# Revit family: Window-NanaWall-HSW-45
name_source: partatom
category: Windows
revit_build: Autodesk Revit Architecture 2013 (Build: 20130531_2115(x64)
units: mm (PartAtom-declared; Revit-internal decimal feet)

## types (1)
- Window_HSW45_NanaWall
    04 CSI = 08 41 13
    95 CSI = 8411
    Assembly Code = B2030110
    Cost Info = http://www.nanawall.com
    Description = Standard Aluminum Framed Single Track Sliding System
    Disclaimer = Please note that the Revit model is for schematic purposes only.  To obtain a detailed 3D model, please go to the NanaWall's configurator at www.nanawall.com.
    Engineering Details URL = http://www.nanawall.com
    Exterior Wall Offset = 0' - 3"
    Filler = Rubber - NanaWall - Black
    Glass Material = Glass - NanaWall - Generic
    Glazing Options = http://www.nanawall.com
    Height = 6' - 8"
    Height Constraint = 6' - 8"
    Horizontal Mullion Height = 3' - 0"
    Installation and Service URL = http://www.nanawall.com
    Manufacturer = NanaWall Systems, Inc.
    Manufacturer Fax = (415) 383-0312
    Max Panel Height = 6' - 6 3/128"
    Model = HSW45
    NanaWall Configurator = http://www.nanawall.com
    Opening Width = 5' - 5 121/256"
    Panel Height = 6' - 6 3/128"
    Performance URL = http://www.nanawall.com
    Product Page URL = http://www.nanawall.com
    Rough Height = 6' - 6 3/128"
    Rough Width = 5' - 8 115/128"
    Sash = Metal - NanaWall - Aluminum
    Sills Available = Raised, Low Profile Saddle, Flush
    Stack Thickness = 0' - 8 1/4"
    Subcategory = Folding Window
    Thickness = 0' - 1 3/8"
    URL = http://www.nanawall.com
    Wall Closure = By host
    Warranty URL = http://www.nanawall.com
    Width = 6' - 0"

## geometry (parser evidence)
native form markers: Blend x4, Sweep x13
no freeform markers — native parametric forms only
